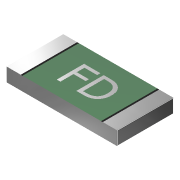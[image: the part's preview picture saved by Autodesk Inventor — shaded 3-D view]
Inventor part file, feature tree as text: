
AUTODESK INVENTOR PART (.ipt)
format: ipt  version: 2012 (Build 160160000, 160)  size: 145,920 bytes
history: native  units: mm
features: extrude x3, sketch x3, plane x1, mirror x1, fillet x1
ambient origin geometry x8: Origin, YZ Plane, XZ Plane, XY Plane, X Axis, Y Axis, Z Axis, Center Point
bodies: Solid1 (feature_tree)
feature tree (9):
  extrude  "Extrusion1"  Depth=3.25mm
  extrude  "Extrusion2"  Depth=0.425mm
  plane  "Work Plane1"
  mirror  "Mirror1"
  sketch  "Sketch3"  dims[d7=0.05mm d8=0.02mm d9=0.001mm d10=0.0mm]
  fillet  "Fillet1"  Radius=0.001mm
  extrude  "Extrusion3"  Depth=0.02mm
  sketch  "Sketch1"  dims[d0=1.65mm d1=3.25mm]
  sketch  "Sketch2"  dims[d2=0.4mm d3=0.0mm d4=0.425mm d5=0.001mm d6=0.0mm]
